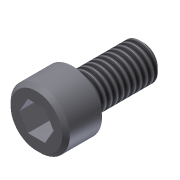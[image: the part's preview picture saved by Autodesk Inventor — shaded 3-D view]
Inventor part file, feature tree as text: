
AUTODESK INVENTOR PART (.ipt)
format: ipt  version: 2013 (Build 170138000, 138)  size: 110,080 bytes
history: native  units: in
note: dims shown in document units (in); Inventor stores cm internally (conversion verified against a paired STEP export)
features: extrude x3, sketch x3, chamfer x2, thread x1
ambient origin geometry x8: Origin, YZ Plane, XZ Plane, XY Plane, X Axis, Y Axis, Z Axis, Center Point
bodies: Solid1 (feature_tree)
feature tree (9):
  extrude  "Extrusion1"  Depth=0.19in TaperAngle=0.0deg
  extrude  "Extrusion2"  Depth=0.375in TaperAngle=0.0deg
  extrude  "Extrusion3"  Depth=0.125in TaperAngle=0.0deg
  thread  "Thread1"  [1 undecoded]
  chamfer  "Chamfer1"  Distance=0.02in Angle=45.0deg
  chamfer  "Chamfer2"  Distance=0.02in Angle=45.0deg
  sketch  "Sketch1"  dims[d0=0.312in d1=0.19in d2=0.0in]
  sketch  "Sketch2"  dims[d3=0.19in d4=0.375in d5=0.0in]
  sketch  "Sketch3"  dims[d6=0.1562in d7=0.125in d8=0.0in d9=1.0in d10=0.0in d11=0.02in d12=0.125in d13=45.0deg d14=0.02in d15=0.125in d16=45.0deg]
note: 1 required parameter value undecoded (feature->parameter linkage not recoverable at this tier; creation-order binding heuristic only, values carry confidence <= 0.55)
